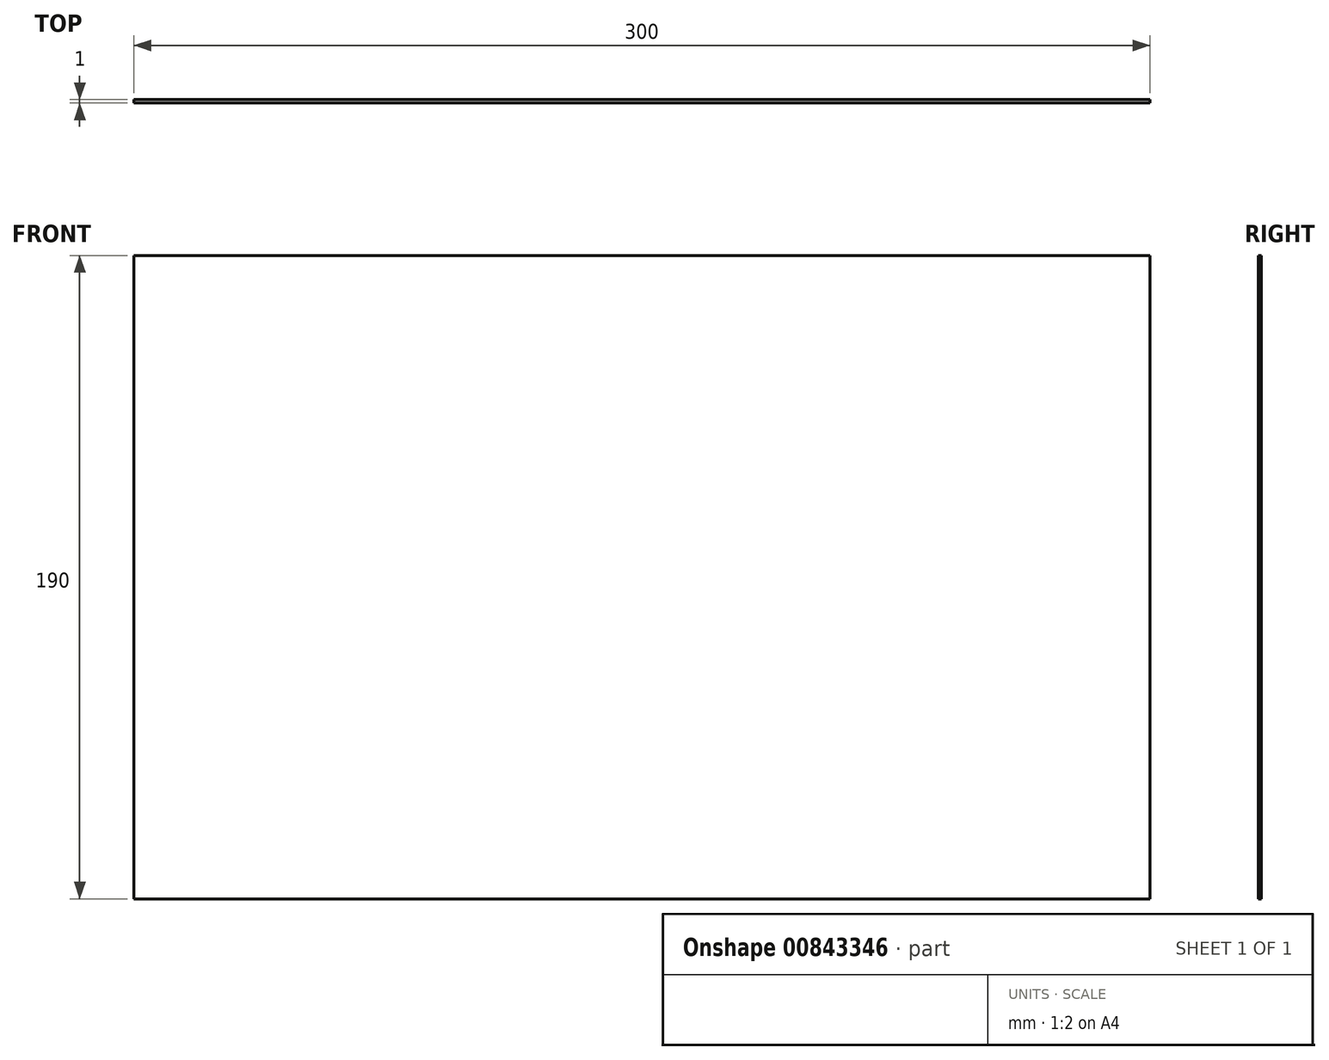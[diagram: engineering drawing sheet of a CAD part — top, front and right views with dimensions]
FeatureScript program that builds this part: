
annotation { "Feature Type Name" : "Feature", "Feature Type Description" : "" }
export const myFeature = defineFeature(function(context is Context, id is Id, definition is map)
    precondition{}
    {
        {
            var Q0;
            Q0=qCreatedBy(makeId("Front.planeOp"),FACE);
            var sketch = newSketch(context, id + "F0", { "sketchPlane" : qUnion([Q0])});
            skLineSegment(sketch, "E0.bottom", {"start": v(150, 95) * mm, "end": v(-150, 95) * mm});
            skLineSegment(sketch, "E0.top", {"start": v(150, -95) * mm, "end": v(-150, -95) * mm});
            skLineSegment(sketch, "E0.left", {"start": v(150, 95) * mm, "end": v(150, -95) * mm});
            skLineSegment(sketch, "E0.right", {"start": v(-150, 95) * mm, "end": v(-150, -95) * mm});
            skPoint(sketch, "E0.middle", {"position": v(0, 0) * mm});
            skSolve(sketch);
        }
        {
            var Q0;
            Q0=qSketchRegion(id+"F0",true);
            extrude(context, id + "F1", {"entities" : qUnion([Q0]), "depth" : 1 * mm, "offsetDistance" : 25 * mm});
        }
    });
